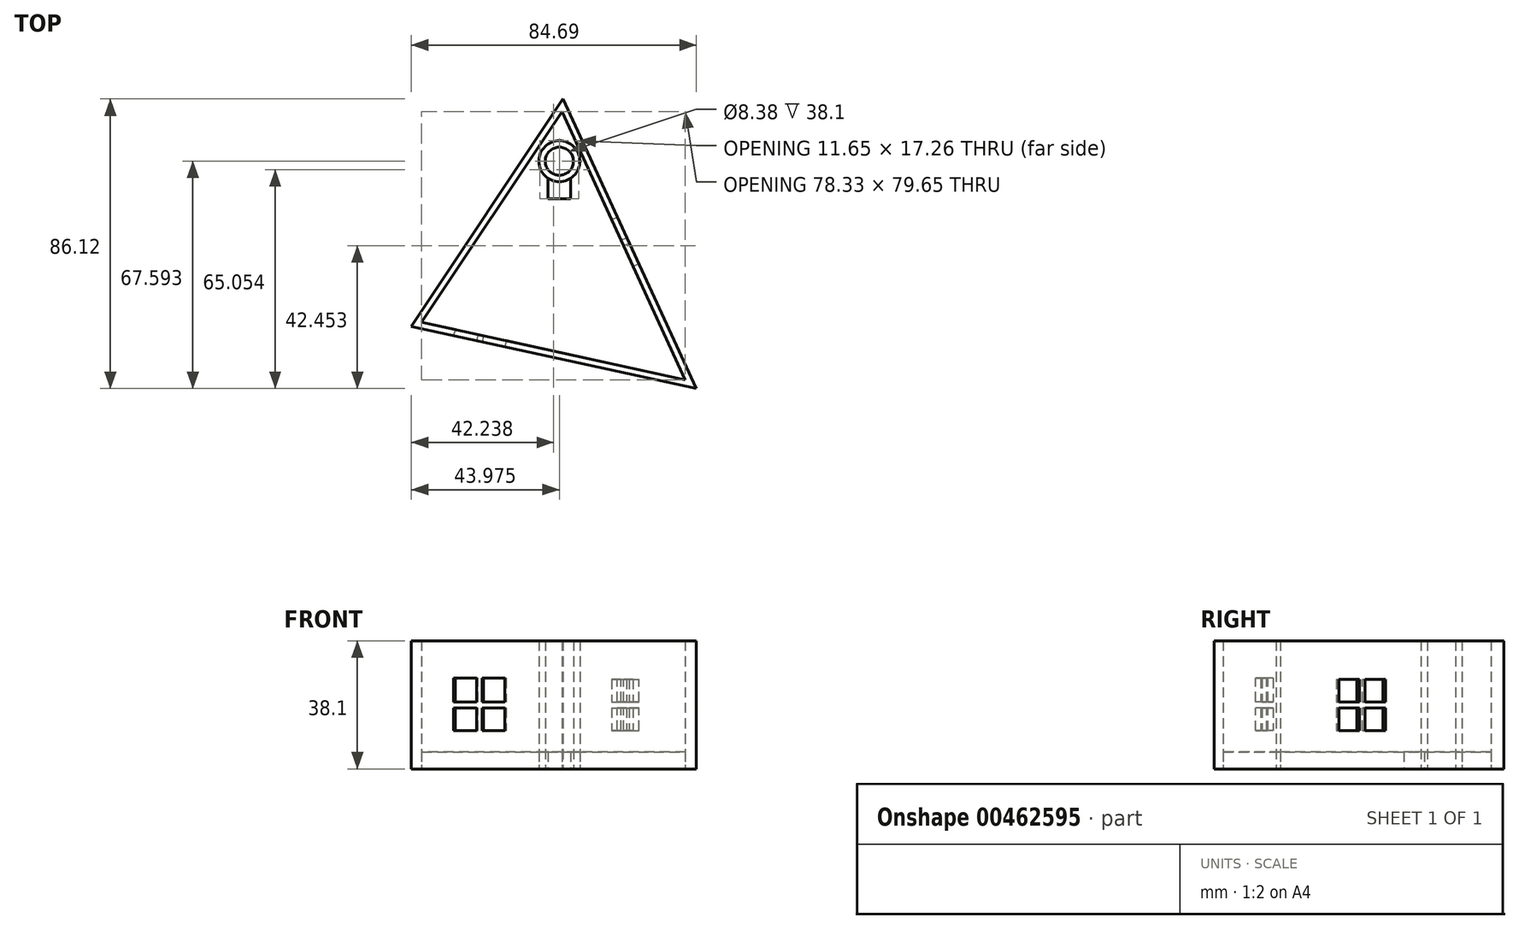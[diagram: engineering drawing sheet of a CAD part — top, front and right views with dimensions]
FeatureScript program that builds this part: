
annotation { "Feature Type Name" : "Feature", "Feature Type Description" : "" }
export const myFeature = defineFeature(function(context is Context, id is Id, definition is map)
    precondition{}
    {
        {
            var Q0;
            Q0=qCreatedBy(makeId("Top.planeOp"),FACE);
            var sketch = newSketch(context, id + "F0", { "sketchPlane" : qUnion([Q0])});
            skLineSegment(sketch, "E0", {"start": v(0, 47.28) * mm, "end": v(-41.66, -15.28) * mm});
            skLineSegment(sketch, "E1", {"start": v(-41.66, -15.28) * mm, "end": v(36.67, -32.37) * mm});
            skLineSegment(sketch, "E2", {"start": v(36.67, -32.37) * mm, "end": v(0, 47.28) * mm});
            skLineSegment(sketch, "E3", {"start": v(-43.22, -14.24) * mm, "end": v(0.3, 51.12) * mm});
            skLineSegment(sketch, "E4", {"start": v(1.72, 48.07) * mm, "end": v(39.96, -35) * mm});
            skLineSegment(sketch, "E5", {"start": v(36.27, -34.2) * mm, "end": v(-44.73, -16.52) * mm});
            skLineSegment(sketch, "E6", {"start": v(-43.22, -14.24) * mm, "end": v(-44.73, -16.52) * mm});
            skLineSegment(sketch, "E7", {"start": v(36.27, -34.2) * mm, "end": v(39.96, -35) * mm});
            skLineSegment(sketch, "E8", {"start": v(1.72, 48.07) * mm, "end": v(0.3, 51.12) * mm});
            skCircle(sketch, "E9", {"center": v(-0.76, 32.6) * mm, "radius": 4.2 * mm});
            skCircle(sketch, "E10", {"center": v(-0.76, 32.6) * mm, "radius": 6.09 * mm});
            skLineSegment(sketch, "E11", {"start": v(-0.76, 19.28) * mm, "end": v(-0.76, 32.6) * mm, "construction": true});
            skLineSegment(sketch, "E12", {"start": v(-4.15, 27.53) * mm, "end": v(-4.15, 21.43) * mm});
            skLineSegment(sketch, "E13", {"start": v(-4.15, 21.43) * mm, "end": v(-0.76, 21.43) * mm});
            skLineSegment(sketch, "E14.MirrorCS", {"start": v(2.64, 27.53) * mm, "end": v(2.64, 21.43) * mm});
            skLineSegment(sketch, "E15.MirrorCS", {"start": v(2.64, 21.43) * mm, "end": v(-0.76, 21.43) * mm});
            skSolve(sketch);
        }
        {
            var Q0;
            Q0=makeQuery(id+"F0.imprint","IMPRINT",FACE,{"disambiguationData":[TD([[makeQuery(id+"F0.imprint","IMPRINT",EDGE,{"derivedFrom":sQuery(id+"F0.wireOp",EDGE,"E0")}),-1.0]])]});
            var Q1;
            Q1=makeQuery(id+"F0.imprint","IMPRINT",FACE,{"disambiguationData":[TD([[makeQuery(id+"F0.imprint","IMPRINT",EDGE,{"derivedFrom":sQuery(id+"F0.wireOp",EDGE,"Oxo17ItW-w14z-22ZS-DC4n-RRN2416DCjXd")}),-1.0]])]});
            var Q2;
            Q2=makeQuery(id+"F0.imprint","IMPRINT",FACE,{"disambiguationData":[TD([[makeQuery(id+"F0.imprint","IMPRINT",EDGE,{"derivedFrom":sQuery(id+"F0.wireOp",EDGE,"E9")}),-1.0]])]});
            extrude(context, id + "F1", {"entities" : qUnion([Q0, Q1, Q2]), "depth" : 38.1 * mm});
        }
        {
            var Q0;
            Q0=makeQuery(id+"F0.imprint","IMPRINT",FACE,{"disambiguationData":[TD([[makeQuery(id+"F0.imprint","IMPRINT",EDGE,{"derivedFrom":sQuery(id+"F0.wireOp",EDGE,"E0")}),1.0]])]});
            extrude(context, id + "F2", {"entities" : qUnion([Q0]), "depth" : 5.08 * mm});
        }
        {
            var Q0;
            Q0=makeQuery(id+"F1.opExtrude","SWEPT_FACE",FACE,{"disambiguationData":[OSD([sQuery(id+"F0.wireOp",EDGE,"E5"),sQuery(id+"F0.wireOp",EDGE,"E7")])]});
            var sketch = newSketch(context, id + "F3", { "sketchPlane" : qUnion([Q0])});
            skLineSegment(sketch, "E16", {"start": v(3.16, 38.1) * mm, "end": v(3.16, 0) * mm, "construction": true});
            skLineSegment(sketch, "E17", {"start": v(-40.18, 19.05) * mm, "end": v(46.5, 19.05) * mm, "construction": true});
            skLineSegment(sketch, "E18", {"start": v(-19.5, 38.36) * mm, "end": v(-19.5, 0) * mm, "construction": true});
            skLineSegment(sketch, "E19.bottom", {"start": v(-11.7, 11.38) * mm, "end": v(-27.3, 11.38) * mm});
            skLineSegment(sketch, "E19.top", {"start": v(-11.7, 26.98) * mm, "end": v(-27.3, 26.98) * mm});
            skLineSegment(sketch, "E19.left", {"start": v(-11.7, 11.38) * mm, "end": v(-11.7, 26.98) * mm});
            skLineSegment(sketch, "E19.right", {"start": v(-27.3, 11.38) * mm, "end": v(-27.3, 26.98) * mm});
            skPoint(sketch, "E19.middle", {"position": v(-19.5, 19.18) * mm});
            skLineSegment(sketch, "E20", {"start": v(-20.4, 26.98) * mm, "end": v(-20.4, 11.38) * mm});
            skLineSegment(sketch, "E21.MirrorCS", {"start": v(-18.61, 26.98) * mm, "end": v(-18.61, 11.38) * mm});
            skLineSegment(sketch, "E22", {"start": v(-20.4, 26.98) * mm, "end": v(-18.61, 26.98) * mm});
            skLineSegment(sketch, "E23", {"start": v(-27.3, 18.16) * mm, "end": v(-11.7, 18.16) * mm});
            skLineSegment(sketch, "E24.MirrorCS", {"start": v(-27.3, 19.94) * mm, "end": v(-11.7, 19.94) * mm});
            skLineSegment(sketch, "E25", {"start": v(-27.3, 19.94) * mm, "end": v(-27.3, 18.16) * mm});
            skLineSegment(sketch, "E26.MirrorCS", {"start": v(18.03, 26.98) * mm, "end": v(33.62, 26.98) * mm});
            skLineSegment(sketch, "E27.MirrorCS", {"start": v(18.03, 11.38) * mm, "end": v(18.03, 26.98) * mm});
            skLineSegment(sketch, "E28.MirrorCS", {"start": v(33.62, 11.38) * mm, "end": v(33.62, 26.98) * mm});
            skLineSegment(sketch, "E29.MirrorCS", {"start": v(18.03, 11.38) * mm, "end": v(33.62, 11.38) * mm});
            skLineSegment(sketch, "E30.MirrorCS", {"start": v(33.62, 18.16) * mm, "end": v(18.03, 18.16) * mm});
            skLineSegment(sketch, "E31.MirrorCS", {"start": v(33.62, 19.94) * mm, "end": v(18.03, 19.94) * mm});
            skLineSegment(sketch, "E32.MirrorCS", {"start": v(26.72, 26.98) * mm, "end": v(26.72, 11.38) * mm});
            skLineSegment(sketch, "E33.MirrorCS", {"start": v(24.94, 26.98) * mm, "end": v(24.94, 11.38) * mm});
            skSolve(sketch);
        }
        {
            var Q0;
            {var subQ0=sQuery(id+"F3.wireOp",EDGE,"E19.right");var subQ1=sQuery(id+"F3.wireOp",EDGE,"E19.top");var subQ2=makeQuery(id+"F3.imprint","INTERSECT",VERTEX,{"derivedFrom":[subQ1,subQ0]});Q0=makeQuery(id+"F3.imprint","IMPRINT",FACE,{"disambiguationData":[TD([[makeQuery(id+"F3.imprint","IMPRINT",EDGE,{"disambiguationData":[TD([[subQ2,1.0]])],"derivedFrom":subQ1}),1.0]])]});}
            var Q1;
            {var subQ0=sQuery(id+"F3.wireOp",EDGE,"E19.right");var subQ1=sQuery(id+"F3.wireOp",EDGE,"E19.bottom");var subQ2=makeQuery(id+"F3.imprint","INTERSECT",VERTEX,{"derivedFrom":[subQ1,subQ0]});Q1=makeQuery(id+"F3.imprint","IMPRINT",FACE,{"disambiguationData":[TD([[makeQuery(id+"F3.imprint","IMPRINT",EDGE,{"disambiguationData":[TD([[subQ2,1.0]])],"derivedFrom":subQ1}),-1.0]])]});}
            var Q2;
            {var subQ0=sQuery(id+"F3.wireOp",EDGE,"E19.left");var subQ1=sQuery(id+"F3.wireOp",EDGE,"E19.bottom");var subQ2=makeQuery(id+"F3.imprint","INTERSECT",VERTEX,{"derivedFrom":[subQ1,subQ0]});Q2=makeQuery(id+"F3.imprint","IMPRINT",FACE,{"disambiguationData":[TD([[makeQuery(id+"F3.imprint","IMPRINT",EDGE,{"disambiguationData":[TD([[subQ2,-1.0]])],"derivedFrom":subQ1}),-1.0]])]});}
            var Q3;
            {var subQ0=sQuery(id+"F3.wireOp",EDGE,"E19.left");var subQ1=sQuery(id+"F3.wireOp",EDGE,"E19.top");var subQ2=makeQuery(id+"F3.imprint","INTERSECT",VERTEX,{"derivedFrom":[subQ1,subQ0]});Q3=makeQuery(id+"F3.imprint","IMPRINT",FACE,{"disambiguationData":[TD([[makeQuery(id+"F3.imprint","IMPRINT",EDGE,{"disambiguationData":[TD([[subQ2,1.0]])],"derivedFrom":subQ0}),1.0]])]});}
            extrude(context, id + "F4", {"entities" : qUnion([Q0, Q1, Q2, Q3]), "operationType" : NewBodyOperationType.REMOVE, "oppositeDirection" : true, "depth" : 1.9 * mm});
        }
        {
            var Q0;
            Q0=makeQuery(id+"F1.opExtrude","SWEPT_FACE",FACE,{"disambiguationData":[OSD([sQuery(id+"F0.wireOp",EDGE,"E4"),sQuery(id+"F0.wireOp",EDGE,"E8")])]});
            var sketch = newSketch(context, id + "F5", { "sketchPlane" : qUnion([Q0])});
            skLineSegment(sketch, "E34", {"start": v(0, 38.1) * mm, "end": v(0, 0) * mm, "construction": true});
            skPoint(sketch, "E34.startSnap0", {"position": v(-1.1, 38.1) * mm});
            skLineSegment(sketch, "E35", {"start": v(-48.5, 19.05) * mm, "end": v(46.3, 19.05) * mm, "construction": true});
            skLineSegment(sketch, "E36.bottom", {"start": v(7.62, 11.43) * mm, "end": v(-7.62, 11.43) * mm});
            skLineSegment(sketch, "E36.top", {"start": v(7.62, 26.67) * mm, "end": v(-7.62, 26.67) * mm});
            skLineSegment(sketch, "E36.left", {"start": v(7.62, 11.43) * mm, "end": v(7.62, 26.67) * mm});
            skLineSegment(sketch, "E36.right", {"start": v(-7.62, 11.43) * mm, "end": v(-7.62, 26.67) * mm});
            skPoint(sketch, "E36.middle", {"position": v(0, 19.05) * mm});
            skLineSegment(sketch, "E37", {"start": v(-0.89, 26.67) * mm, "end": v(-0.89, 11.43) * mm});
            skLineSegment(sketch, "E38", {"start": v(-7.62, 19.94) * mm, "end": v(7.62, 19.94) * mm});
            skLineSegment(sketch, "E39.MirrorCS", {"start": v(0.89, 26.67) * mm, "end": v(0.89, 11.43) * mm});
            skLineSegment(sketch, "E40.MirrorCS", {"start": v(-7.62, 18.16) * mm, "end": v(7.62, 18.16) * mm});
            skSolve(sketch);
        }
        {
            var Q0;
            {var subQ0=sQuery(id+"F5.wireOp",EDGE,"E36.right");var subQ1=sQuery(id+"F5.wireOp",EDGE,"E36.top");var subQ2=makeQuery(id+"F5.imprint","INTERSECT",VERTEX,{"derivedFrom":[subQ1,subQ0]});Q0=makeQuery(id+"F5.imprint","IMPRINT",FACE,{"disambiguationData":[TD([[makeQuery(id+"F5.imprint","IMPRINT",EDGE,{"disambiguationData":[TD([[subQ2,1.0]])],"derivedFrom":subQ1}),1.0]])]});}
            var Q1;
            {var subQ0=sQuery(id+"F5.wireOp",EDGE,"E36.right");var subQ1=sQuery(id+"F5.wireOp",EDGE,"E36.bottom");var subQ2=makeQuery(id+"F5.imprint","INTERSECT",VERTEX,{"derivedFrom":[subQ1,subQ0]});Q1=makeQuery(id+"F5.imprint","IMPRINT",FACE,{"disambiguationData":[TD([[makeQuery(id+"F5.imprint","IMPRINT",EDGE,{"disambiguationData":[TD([[subQ2,1.0]])],"derivedFrom":subQ1}),-1.0]])]});}
            var Q2;
            {var subQ0=sQuery(id+"F5.wireOp",EDGE,"E36.left");var subQ1=sQuery(id+"F5.wireOp",EDGE,"E36.bottom");var subQ2=makeQuery(id+"F5.imprint","INTERSECT",VERTEX,{"derivedFrom":[subQ1,subQ0]});Q2=makeQuery(id+"F5.imprint","IMPRINT",FACE,{"disambiguationData":[TD([[makeQuery(id+"F5.imprint","IMPRINT",EDGE,{"disambiguationData":[TD([[subQ2,-1.0]])],"derivedFrom":subQ1}),-1.0]])]});}
            var Q3;
            {var subQ0=sQuery(id+"F5.wireOp",EDGE,"E36.left");var subQ1=sQuery(id+"F5.wireOp",EDGE,"E36.top");var subQ2=makeQuery(id+"F5.imprint","INTERSECT",VERTEX,{"derivedFrom":[subQ1,subQ0]});Q3=makeQuery(id+"F5.imprint","IMPRINT",FACE,{"disambiguationData":[TD([[makeQuery(id+"F5.imprint","IMPRINT",EDGE,{"disambiguationData":[TD([[subQ2,-1.0]])],"derivedFrom":subQ1}),1.0]])]});}
            extrude(context, id + "F6", {"entities" : qUnion([Q0, Q1, Q2, Q3]), "operationType" : NewBodyOperationType.REMOVE, "oppositeDirection" : true, "depth" : 2.54 * mm});
        }
    });
